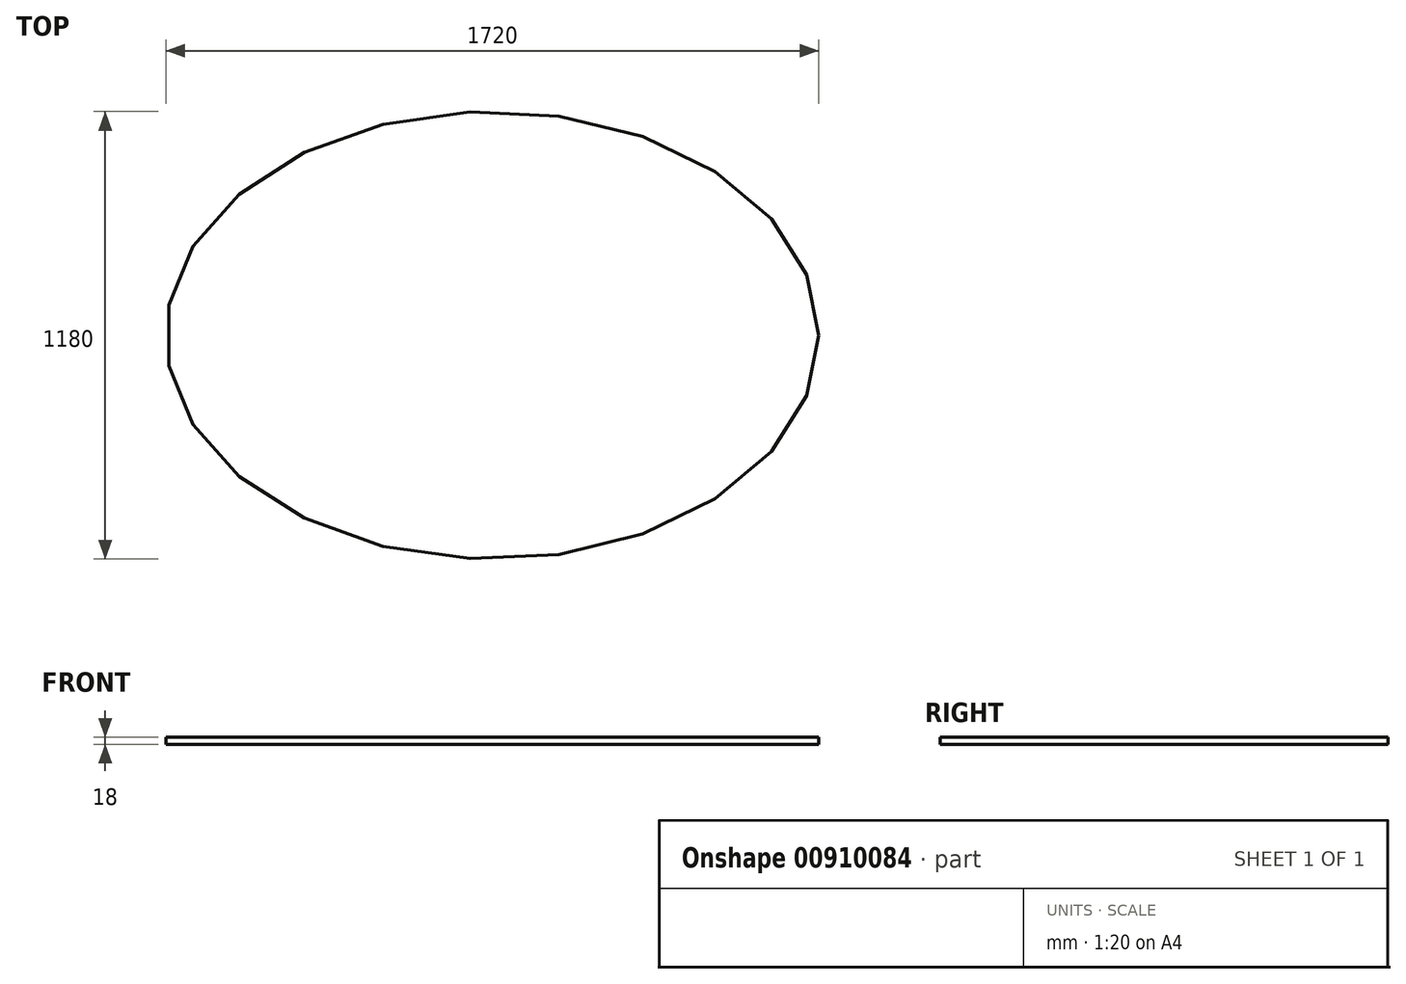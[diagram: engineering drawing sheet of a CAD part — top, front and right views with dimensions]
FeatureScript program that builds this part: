
annotation { "Feature Type Name" : "Feature", "Feature Type Description" : "" }
export const myFeature = defineFeature(function(context is Context, id is Id, definition is map)
    precondition{}
    {
        {
            var Q0;
            Q0=qCreatedBy(makeId("Top.planeOp"),FACE);
            var sketch = newSketch(context, id + "F0", { "sketchPlane" : qUnion([Q0])});
            skEllipse(sketch, "E0", {"center": v(0, 0) * mm, "majorRadius": 860 * mm, "minorRadius": 590 * mm, "majorAxis": v(1, 0)});
            skSolve(sketch);
        }
        {
            var Q0;
            Q0 = qSketchRegion(id + "F0", true);
            extrude(context, id + "F1", {"entities" : qUnion([Q0]), "depth" : 18 * mm, "offsetDistance" : 25 * mm});
        }
    });
